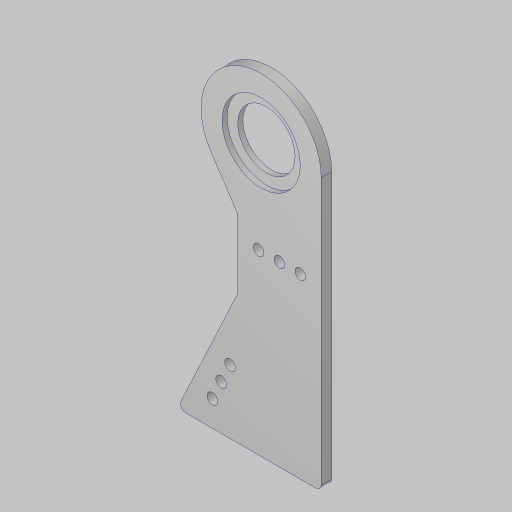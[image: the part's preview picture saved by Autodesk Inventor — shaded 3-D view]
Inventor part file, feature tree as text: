
AUTODESK INVENTOR PART (.ipt)
format: ipt  version: 2023.5 (Build 275446000, 446)  size: 246,784 bytes
history: native  units: in
note: dims shown in document units (in); Inventor stores cm internally (conversion verified against a paired STEP export)
features: sketch x3, extrude x2, projected_geometry x2, hole x1, fillet x1
ambient origin geometry x8: Origin, YZ Plane, XZ Plane, XY Plane, X Axis, Y Axis, Z Axis, Center Point
bodies: Solid1 (feature_tree)
feature tree (9):
  sketch  "Sketch1"  dims[d0=1.875in d1=0.5in]
  extrude  "Extrusion1"  Depth=0.5in
  hole  "Hole1"  [1 undecoded]
  extrude  "Extrusion2"  Depth=0.125in
  sketch  "Sketch3"  dims[d4=2.0in d5=15.25in d6=1.0in d7=0.1718in d8=15.0in d10=1.0in d11=2.75in d13=17.0in d15=7.375in d17=0.5in d18=0.5in d19=0.5in d20=0.5in d21=1.9685in d23=0.5in d24=0.3937in d26=1.0in d28=0.25in d29=0.0in d30=0.26in d31=0.75in d32=0.385in d33=0.25in d34=0.5635in d35=1.0in d36=0.8108in d37=0.25in d38=0.125in d39=0.0in d40=0.125in]
  fillet  "Fillet1"  Radius=1.0in
  sketch  "Sketch2"  dims[d2=2.0in d3=6.5in]
  projected_geometry  "Project Cut Edges1"
  projected_geometry  "Project Cut Edges2"
note: 1 required parameter value undecoded (feature->parameter linkage not recoverable at this tier; creation-order binding heuristic only, values carry confidence <= 0.55)
